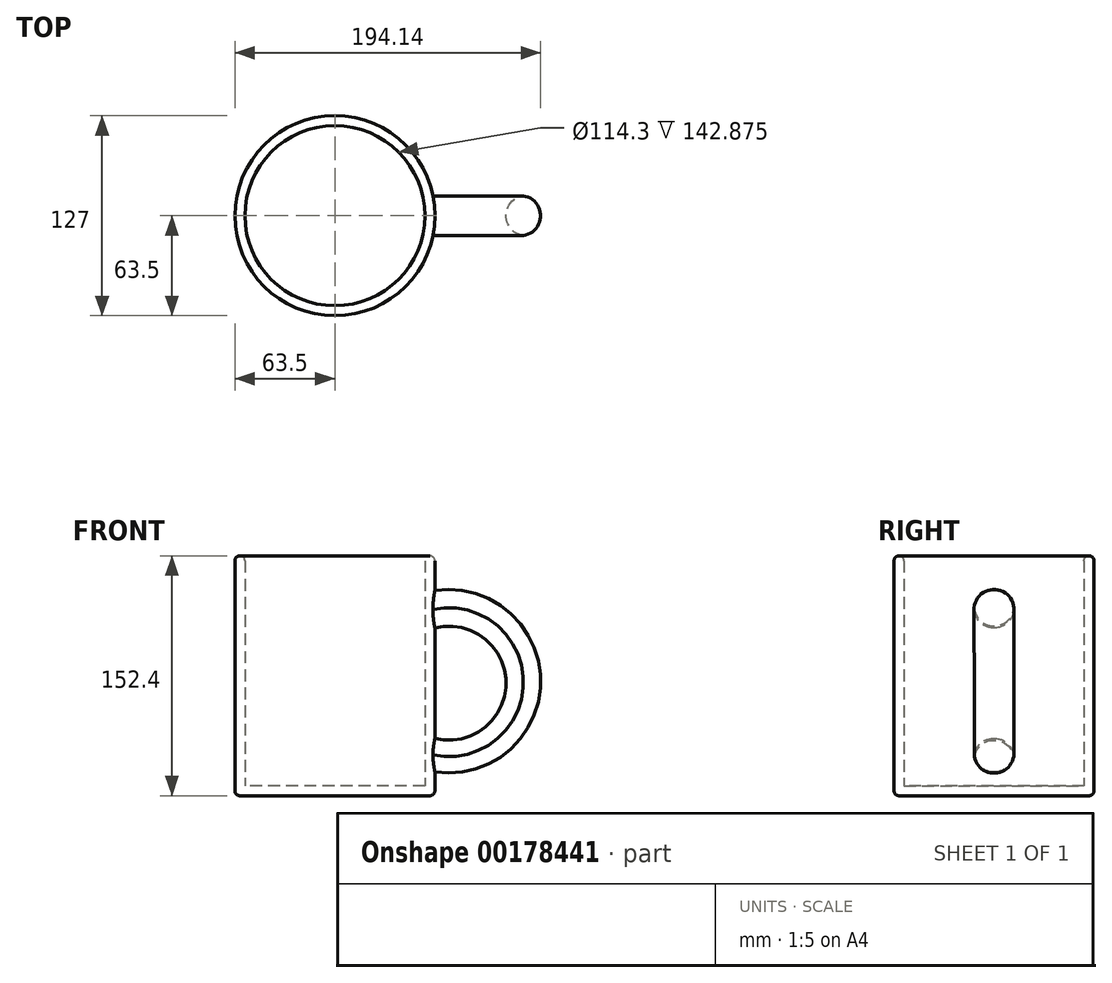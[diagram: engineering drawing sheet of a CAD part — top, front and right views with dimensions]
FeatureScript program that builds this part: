
annotation { "Feature Type Name" : "Feature", "Feature Type Description" : "" }
export const myFeature = defineFeature(function(context is Context, id is Id, definition is map)
    precondition{}
    {
        {
            var Q0;
            Q0=qCreatedBy(makeId("Top.planeOp"),FACE);
            var sketch = newSketch(context, id + "F0", { "sketchPlane" : qUnion([Q0])});
            skCircle(sketch, "E0", {"center": v(0, 0) * mm, "radius": 63.5 * mm});
            skSolve(sketch);
        }
        {
            var Q0;
            Q0=qCreatedBy(makeId("Front.planeOp"),FACE);
            var sketch = newSketch(context, id + "F1", { "sketchPlane" : qUnion([Q0])});
            skArc(sketch, "E1", {"start": v(49.5, 19) * mm, "mid": v(130.64, 72.7) * mm, "end": v(49.5, 126.41) * mm});
            skLineSegment(sketch, "E2", {"start": v(49.5, 126.41) * mm, "end": v(49.5, 99.53) * mm});
            skLineSegment(sketch, "E3", {"start": v(49.5, 19) * mm, "end": v(49.5, 43.55) * mm});
            skArc(sketch, "E4", {"start": v(49.5, 43.55) * mm, "mid": v(108.72, 71.54) * mm, "end": v(49.5, 99.53) * mm});
            skSolve(sketch);
        }
        {
            var Q0;
            Q0=makeQuery(id+"F0.imprint","IMPRINT",FACE,{"disambiguationData":[TD([[makeQuery(id+"F0.imprint","IMPRINT",EDGE,{"derivedFrom":sQuery(id+"F0.wireOp",EDGE,"E0")}),1.0]])]});
            extrude(context, id + "F2", {"entities" : qUnion([Q0]), "depth" : 152.4 * mm});
        }
        {
            var Q0;
            Q0=makeQuery(id+"F2.opExtrude","CAP_FACE",FACE,{"disambiguationData":[OSD([sQuery(id+"F0.wireOp",EDGE,"E0")])],"isStart":false});
            shell(context, id + "F3", {"entities" : qUnion([Q0]), "thickness" : 6.35 * mm});
        }
        {
            var Q0;
            Q0=makeQuery(id+"F1.imprint","IMPRINT",FACE,{"disambiguationData":[TD([[makeQuery(id+"F1.imprint","IMPRINT",EDGE,{"derivedFrom":sQuery(id+"F1.wireOp",EDGE,"E1")}),1.0]])]});
            extrude(context, id + "F4", {"entities" : qUnion([Q0]), "operationType" : NewBodyOperationType.ADD, "endBound" : BoundingType.SYMMETRIC, "depth" : 25.4 * mm});
        }
        {
            var Q0;
            {var subQ0=sQuery(id+"F0.wireOp",EDGE,"E0");Q0=makeQuery(id+"F3.opShell","OFFSET_FACE",FACE,{"disambiguationData":[OSD([subQ0]),TDD([makeQuery(id+"F2.opExtrude","CAP_FACE",FACE,{"disambiguationData":[OSD([subQ0])],"isStart":true})])]});}
            extrude(context, id + "F5", {"entities" : qUnion([Q0]), "operationType" : NewBodyOperationType.REMOVE, "depth" : 152.4 * mm});
        }
        {
            var Q0;
            {var subQ0=sQuery(id+"F1.wireOp",EDGE,"E1");Q0=makeQuery(id+"F4.boolean.opBoolean","SPLIT",EDGE,{"disambiguationData":[TD([makeQuery(id+"F2.opExtrude","SWEPT_FACE",FACE,{"disambiguationData":[OSD([sQuery(id+"F0.wireOp",EDGE,"E0")])]})])],"derivedFrom":makeQuery(id+"F4.opExtrude","CAP_EDGE",EDGE,{"disambiguationData":[OSD([subQ0])],"isStart":false})});}
            var Q1;
            {var subQ0=sQuery(id+"F1.wireOp",EDGE,"E1");Q1=makeQuery(id+"F4.boolean.opBoolean","SPLIT",EDGE,{"disambiguationData":[TD([makeQuery(id+"F2.opExtrude","SWEPT_FACE",FACE,{"disambiguationData":[OSD([sQuery(id+"F0.wireOp",EDGE,"E0")])]})])],"derivedFrom":makeQuery(id+"F4.opExtrude","CAP_EDGE",EDGE,{"disambiguationData":[OSD([subQ0])],"isStart":true})});}
            var Q2;
            {var subQ0=sQuery(id+"F1.wireOp",EDGE,"E4");Q2=makeQuery(id+"F4.boolean.opBoolean","SPLIT",EDGE,{"disambiguationData":[TD([makeQuery(id+"F2.opExtrude","SWEPT_FACE",FACE,{"disambiguationData":[OSD([sQuery(id+"F0.wireOp",EDGE,"E0")])]})])],"derivedFrom":makeQuery(id+"F4.opExtrude","CAP_EDGE",EDGE,{"disambiguationData":[OSD([subQ0])],"isStart":false})});}
            var Q3;
            {var subQ0=sQuery(id+"F1.wireOp",EDGE,"E4");Q3=makeQuery(id+"F4.boolean.opBoolean","SPLIT",EDGE,{"disambiguationData":[TD([makeQuery(id+"F2.opExtrude","SWEPT_FACE",FACE,{"disambiguationData":[OSD([sQuery(id+"F0.wireOp",EDGE,"E0")])]})])],"derivedFrom":makeQuery(id+"F4.opExtrude","CAP_EDGE",EDGE,{"disambiguationData":[OSD([subQ0])],"isStart":true})});}
            fillet(context, id + "F6", {"entities" : qUnion([Q0, Q1, Q2, Q3]), "radius" : 12.7 * mm, "tangentPropagation" : true, "allowEdgeOverflow" : false});
        }
        {
            var Q0;
            Q0=makeQuery(id+"F2.opExtrude","CAP_EDGE",EDGE,{"disambiguationData":[OSD([sQuery(id+"F0.wireOp",EDGE,"E0")])],"isStart":false});
            var Q1;
            {var subQ0=sQuery(id+"F0.wireOp",EDGE,"E0");Q1=makeQuery(id+"F3.opShell","OFFSET_EDGE",EDGE,{"disambiguationData":[OSD([subQ0]),TDD([makeQuery(id+"F2.opExtrude","CAP_EDGE",EDGE,{"disambiguationData":[OSD([subQ0])],"isStart":false})])]});}
            var Q2;
            Q2=makeQuery(id+"F2.opExtrude","CAP_EDGE",EDGE,{"disambiguationData":[OSD([sQuery(id+"F0.wireOp",EDGE,"E0")])],"isStart":true});
            fillet(context, id + "F7", {"entities" : qUnion([Q0, Q1, Q2]), "radius" : 3.17 * mm, "tangentPropagation" : true, "allowEdgeOverflow" : false});
        }
    });
